# Revit family: NBS_Senator_DmstcChrs_Roam
name_source: partatom
category: Furniture
revit_build: Autodesk Revit 2018 (Build: 20190510_1515(x64)
units: mm (PartAtom-declared; Revit-internal decimal feet)

## family parameters
Always vertical = Yes
Cut with Voids When Loaded = No
Room Calculation Point = No
Shared = No
Work Plane-Based = No

## types (2) — shared parameters
Application = Office and educational settings
AssetType = Fixed
Category = Pr_40_50_12_22:Dining chairs
CodePerformance = ISO 9001, 14001, 18001
Color = Black, Flint Grey, Sage, Coral, White, Pastel Blue, Pale Green
DurationUnit = year
ExpectedLife = 10
Features = Fully upholstered seat, Tubular steel frame in a choice of colours, 50 mm hard wheel catsors
Finish = Flint grey, sage, coral, white, pastel blue, pale green
FramesColour = Black
IfcExportAs = IfcFurnitureType
IfcExportType = STOOL
IsBuiltIn = No
ManufacturerName = The Senator Group
ManufacturerURL = www.senator.co.uk
Material = Fabric, metal, plastic
NBSCertification = www.nationalbimlibrary.com/cert/44pxi1os
NBSDescription = Domestic chairs
NBSReference = 45-35-20/365
NominalDepth = 330 mm  [stored 1.08268 ft]
NominalLength = 455 mm
NominalWidth = 455 mm
OptionalExtras = Choice of finish options available, 50 mm Black soft wheel castors
ProductInformation = http://www.thesenatorgroup.com
SeatDepth = 330 mm  [stored 1.08268 ft]
SeatMaterial = NBS_Senator_Leather_DarkBrown
SeatWidth = 455 mm
Shape = Round
SpecifiableFeatures = 2 Seat heights, Tubular steel frame, 50 mm hard wheel castors, Upholstered seat with raised peripheral seam detail (fabric upholstery only)
Status = UNSET
SteelFrameMaterial = NBS_Senator_Aluminium_Rigid_Black
Style = Stool
SustainabilityPerformance = FSC certified
Uniclass2015Code = Pr_40_50_12_22
Uniclass2015Title = Dining chairs
Uniclass2015Version = Products v1.16
Version = 1
WarrantyDescription = Senator warrants that its manufactured products are free from manufacturing defects - in materials or workmanship - for a period of ten (10) years on Senator Seating ranges; and fifteen (15) years on Senator Desking ranges - exceptions are listed below. Senator will repair or replace (at Senator’s sole discretion) with comparable free of charge materials / components, any product / component, which fails under normal use in a single shift environment, as a result of a defect in the materials and / or workmanship
WarrantyDurationParts = 10
WarrantyDurationUnit = year
zero-valued in all types: HighestSeatingHeight, LowestSeatingHeight, SeatingHeight

## per-type parameters (varying)
| type | BIMObjectName | Description | ModelReference | Name | NominalHeight | SeatHeight | Size | Weight | WheelCastorMaterial |
| ROM01 | NBS_Senator_DomesticChairs_Roam_ROM01 | Low mobile stool | Roam_ROM01 | DomesticChairs_Roam_ROM01_Senator | 500 mm  [stored 1.64042 ft] | 500 mm  [stored 1.64042 ft] | 330 x 500 x 455 mm | 4 kg | NBS_SenatorGroup_Plastic_Black |
| ROM02 | NBS_Senator_DomesticChairs_Roam_ROM02 | High mobile stool | Roam_ROM02 | DomesticChairs_Roam_ROM02_Senator | 590 mm  [stored 1.9357 ft] | 590 mm  [stored 1.9357 ft] | 330 x 590 x 455 mm | 4.5 kg | NBS_Senator_Aluminium_Rigid_Black |

note: column(s) folded — value = type name in every type: ModelNumber

note: [stored X ft] marks values corroborated as IEEE doubles in the binary element streams (Revit-internal decimal feet)

## geometry (parser evidence)
native form markers: Sweep x8
no freeform markers — native parametric forms only
